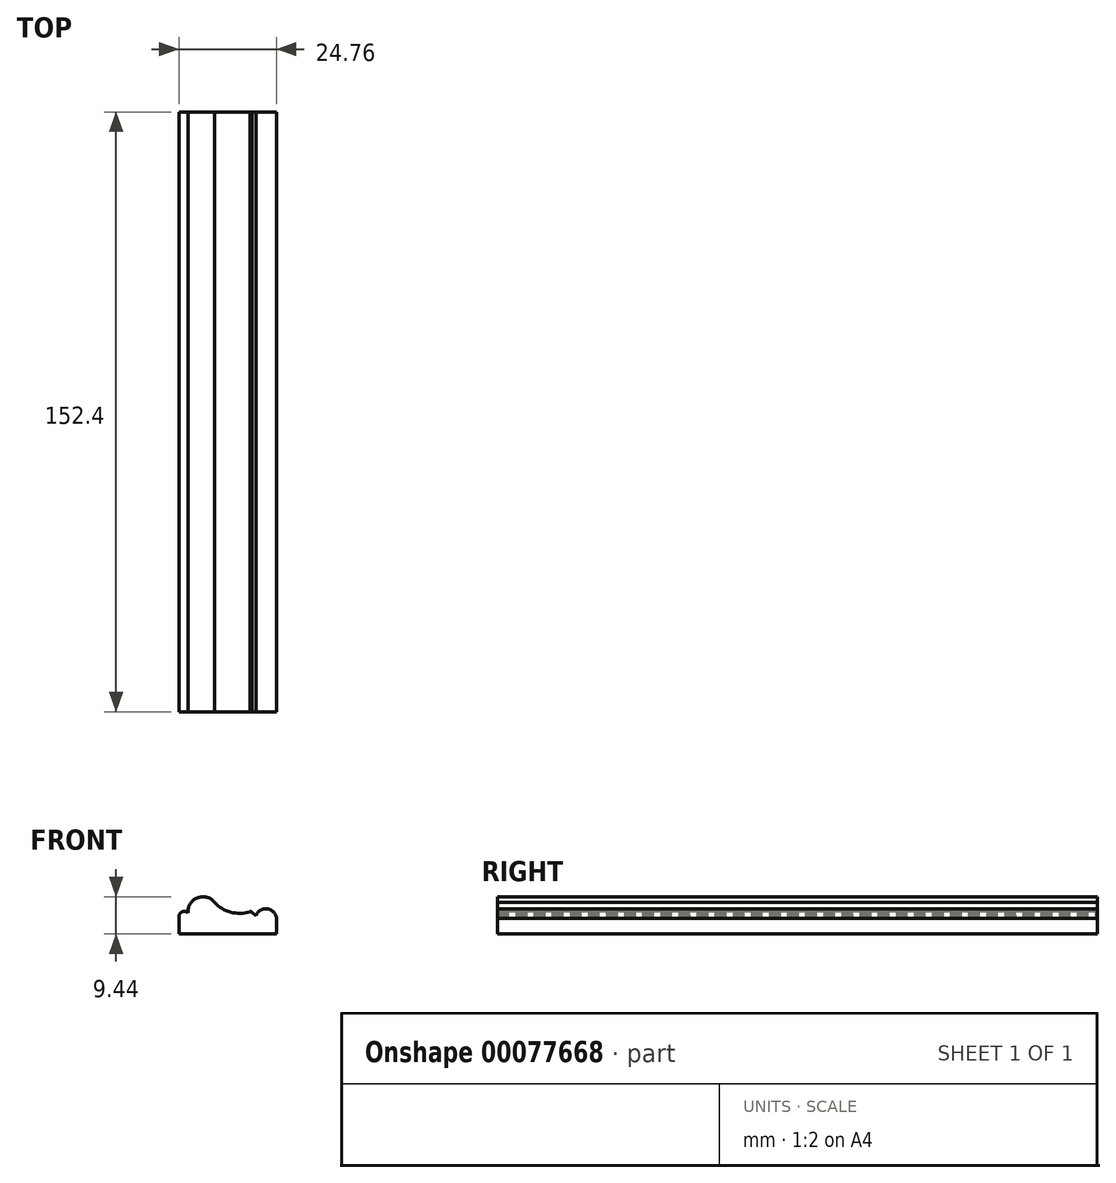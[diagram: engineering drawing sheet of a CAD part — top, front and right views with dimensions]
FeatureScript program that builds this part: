
annotation { "Feature Type Name" : "Feature", "Feature Type Description" : "" }
export const myFeature = defineFeature(function(context is Context, id is Id, definition is map)
    precondition{}
    {
        {
            var Q0;
            Q0=qCreatedBy(makeId("Front.planeOp"),FACE);
            var sketch = newSketch(context, id + "F0", { "sketchPlane" : qUnion([Q0])});
            skLineSegment(sketch, "E0", {"start": v(-12.38, -4.72) * mm, "end": v(-12.38, -0.02) * mm});
            skLineSegment(sketch, "E1", {"start": v(-12.38, -4.72) * mm, "end": v(12.38, -4.72) * mm});
            skLineSegment(sketch, "E2", {"start": v(12.38, -4.72) * mm, "end": v(12.38, -0.72) * mm});
            skLineSegment(sketch, "E3", {"start": v(-12.38, -0.02) * mm, "end": v(-12.38, -4.72) * mm});
            skArc(sketch, "E4", {"start": v(-10.1, 0.65) * mm, "mid": v(-11.44, 0.96) * mm, "end": v(-12.38, -0.02) * mm});
            skArc(sketch, "E5", {"start": v(12.38, -0.72) * mm, "mid": v(10, 1.69) * mm, "end": v(7.14, -0.16) * mm});
            skArc(sketch, "E6", {"start": v(-3.34, 3.33) * mm, "mid": v(-7.7, 4.45) * mm, "end": v(-10.1, 0.65) * mm});
            skArc(sketch, "E7", {"start": v(-3.34, 3.33) * mm, "mid": v(0.8, 0.8) * mm, "end": v(5.64, 0.94) * mm});
            skLineSegment(sketch, "E8", {"start": v(7.14, -0.16) * mm, "end": v(6.17, 0.81) * mm});
            skArc(sketch, "E9", {"start": v(6.17, 0.81) * mm, "mid": v(5.92, 0.96) * mm, "end": v(5.64, 0.94) * mm});
            skSolve(sketch);
        }
        {
            var Q0;
            Q0=makeQuery(id+"F0.imprint","IMPRINT",FACE,{"disambiguationData":[TD([[makeQuery(id+"F0.imprint","IMPRINT",EDGE,{"derivedFrom":sQuery(id+"F0.wireOp",EDGE,"E1")}),1.0]])]});
            extrude(context, id + "F1", {"entities" : qUnion([Q0]), "depth" : 152.4 * mm});
        }
    });
